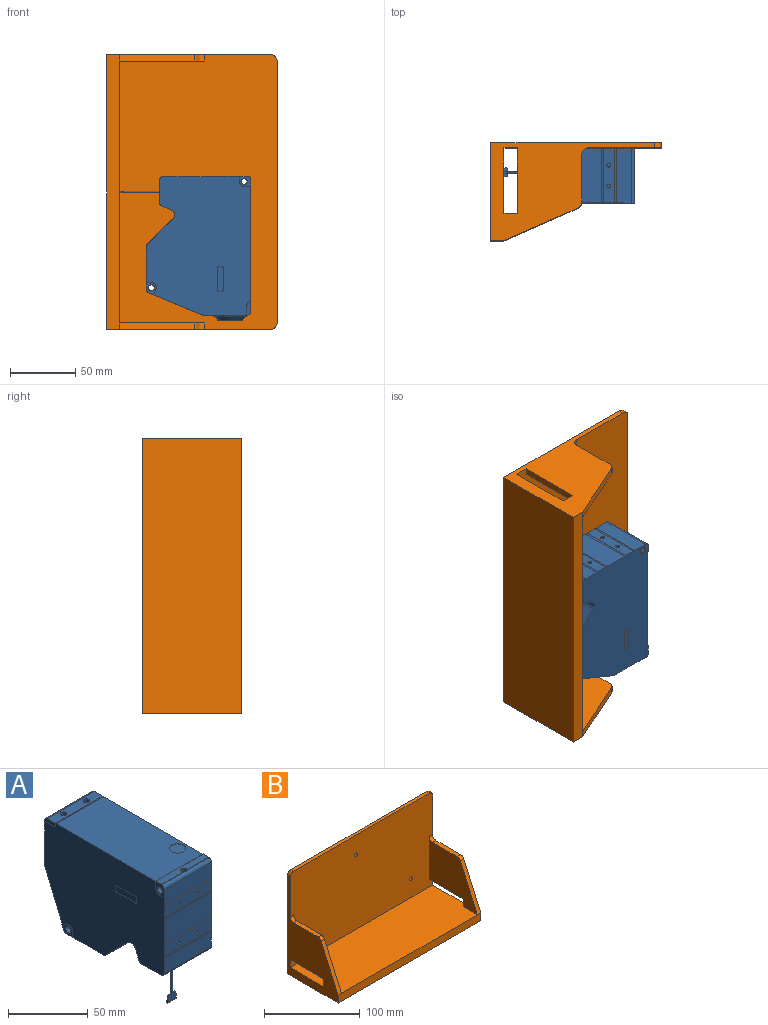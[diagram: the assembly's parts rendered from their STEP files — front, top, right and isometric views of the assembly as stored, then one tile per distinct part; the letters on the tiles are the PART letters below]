
ASSEMBLY  parts=2 mates=3
PART A: 155 faces, bbox 42x110x102.6 mm
  f0: plane 5.2x1mm, normal (-1,0,0.1), area 5.2mm2, adj f1,f4,f7,f8
  f1: plane 2.69x1mm, normal (0,0,1), area 2.6mm2, adj f0,f7,f8,f11
  f2: plane 2.69x1mm, normal (0,0,1), area 2.6mm2, adj f3,f6,f9,f11
  f3: plane 5.2x1mm, normal (1,0,0.1), area 5.2mm2, adj f2,f4,f6,f9
  f4: plane 7.5x1.5mm, normal (0,0,-1), area 7.9mm2, adj f0,f3,f6,f7,f8,f9,f11
  f5: plane 16x16mm, normal (0,1,0), area 201.1mm2, adj f10
  f6: plane 5.2x3.19mm, normal (0,1,0), area 15.3mm2, adj f2,f3,f4,f11
  f7: plane 5.2x3.19mm, normal (0,1,0), area 15.3mm2, adj f0,f1,f4,f11
  f8: plane 5.2x3.19mm, normal (0,-1,0), area 15.3mm2, adj f0,f1,f4,f11
  f9: plane 5.2x3.19mm, normal (0,-1,0), area 15.3mm2, adj f2,f3,f4,f11
  f10: cylinder r=8mm len=16mm, axis (0,-1,0), area 201.1mm2, adj f5,f12
  f11: cylinder r=0.75mm len=33.1mm, axis (0,0,1), area 144.6mm2, adj f1,f2,f4,f6,f7,f8,f9,f13
  f12: plane 18.59x18.59mm, normal (0,1,0), area 67.7mm2, adj f10,f15
  f13: plane 15x3mm, normal (0,0,-1), area 43.2mm2, adj f11,f18,f19,f20,f21
  f14: plane 20x14.14mm, normal (0,-0.71,-0.71), area 314.2mm2, adj f22
  f15: torus R=9.29mm, axis (0,-1,0), area 23.4mm2, adj f12,f23
  f16: plane 4x4mm, normal (0,0,1), area 12.6mm2, adj f25
  f17: plane 4x4mm, normal (0,0,1), area 12.6mm2, adj f26
  f18: plane 3x0.1mm, normal (-1,0,0), area 0.3mm2, adj f13,f19,f21,f39
  f19: plane 15x0.1mm, normal (0,-1,0), area 1.5mm2, adj f13,f18,f20,f39
  f20: plane 3x0.1mm, normal (1,0,0), area 0.3mm2, adj f13,f19,f21,f39
  f21: plane 15x0.1mm, normal (0,1,0), area 1.5mm2, adj f13,f18,f20,f39
  f22: cylinder r=10mm len=20mm, axis (0,-0.71,-0.71), area 6.3mm2, adj f14,f40
  f23: cone r=12.35mm half-angle=45deg, axis (0,-1,0), area 264.6mm2, adj f15,f46
  f24: plane 18.5x5mm, normal (-1,0,0), area 91.6mm2, adj f56,f57,f58,f59,f60,f61,f62,f63
  f25: cylinder r=2mm len=4.7mm, axis (0,0,1), area 59.1mm2, adj f16,f65
  f26: cylinder r=2mm len=4.7mm, axis (0,0,1), area 59.1mm2, adj f17,f65
  f27: plane 10x10mm, normal (0,0,1), area 78.5mm2, adj f68
  f28: plane 20.14x0.35mm, normal (0,-0.26,0.97), area 7.1mm2, adj f29,f32,f69,f70
  f29: cylinder r=2mm len=4.08mm, axis (0,0,1), area 42.1mm2, adj f28,f30,f31,f32,f69
  f30: plane 20.14x0.35mm, normal (0,-0.26,0.97), area 7.1mm2, adj f29,f32,f69,f71
  f31: cylinder r=2.2mm len=42mm, axis (-1,0,0), area 565.9mm2, adj f29,f70,f71
  f32: plane 42x5.01mm, normal (0,0,1), area 198.7mm2, adj f28,f29,f30,f67,f70,f71
  f33: plane 3x3mm, normal (0,-1,0), area 7.1mm2, adj f73
  f34: plane 3x3mm, normal (0,-1,0), area 7.1mm2, adj f74
  f35: plane 3x3mm, normal (0,-1,0), area 7.1mm2, adj f77
  f36: plane 3x3mm, normal (0,-1,0), area 7.1mm2, adj f78
  f37: plane 17.29x1.39mm, normal (0,0,-1), area 24mm2, adj f80,f82,f83,f84
  f38: plane 17.29x5.19mm, normal (0,0,-1), area 89.7mm2, adj f81,f85,f86,f87
  f39: plane 19.8x13.8mm, normal (0,0,-1), area 228.2mm2, adj f18,f19,f20,f21,f88,f89,f90,f91
  f40: plane 26x18.38mm, normal (0,-0.71,-0.71), area 361.8mm2, adj f22,f92,f93,f94,f95
  f41: plane 32.61x7mm, normal (0,0,-1), area 228.3mm2, adj f96,f97,f98,f99
  f42: plane 32.61x5mm, normal (0,0,-1), area 163mm2, adj f100,f101,f102,f103
  f43: plane 27.63x11.45mm, normal (0,0.92,-0.38), area 104.7mm2, adj f104,f105,f106,f107
  f44: cylinder r=2.2mm len=42mm, axis (-1,0,0), area 580.6mm2, adj f109,f110
  f45: plane 27.63x11.45mm, normal (0,0.92,-0.38), area 104.7mm2, adj f111,f112,f113,f114
  f46: torus R=12mm, axis (0,-1,0), area 30.7mm2, adj f23,f115
  f47: plane 3.81x0.2mm, normal (0,-1,0), area 0.8mm2, adj f48,f110,f116,f139
  f48: cylinder r=3.75mm len=5.18mm, axis (1,0,0), area 1.5mm2, adj f47,f49,f110,f116
  f49: plane 4.14x1.71mm, normal (0,0.38,0.92), area 0.9mm2, adj f48,f110,f116,f143
  f50: plane 8x0.2mm, normal (0,0,-1), area 1.6mm2, adj f51,f64,f116,f144
  f51: cylinder r=2mm len=2mm, axis (1,0,0), area 0.6mm2, adj f50,f52,f64,f116
  f52: plane 0.8x0.2mm, normal (0,-1,0), area 0.2mm2, adj f51,f64,f66,f116
  f53: plane 4.81x0.2mm, normal (0,1,0), area 1mm2, adj f54,f67,f71,f116
  f54: cylinder r=3.75mm len=3.75mm, axis (1,0,0), area 1.2mm2, adj f53,f55,f71,f116
  f55: plane 3.8x0.2mm, normal (0,0,-1), area 0.8mm2, adj f54,f71,f116,f127
  f56: plane 3x0.1mm, normal (0,-1,0), area 0.3mm2, adj f24,f57,f63,f116
  f57: cylinder r=1mm len=1mm, axis (-1,0,0), area 0.2mm2, adj f24,f56,f58,f116
  f58: plane 16.5x0.1mm, normal (0,0,1), area 1.6mm2, adj f24,f57,f59,f116
  f59: cylinder r=1mm len=1mm, axis (-1,0,0), area 0.2mm2, adj f24,f58,f60,f116
  f60: plane 3x0.1mm, normal (0,1,0), area 0.3mm2, adj f24,f59,f61,f116
  f61: cylinder r=1mm len=1mm, axis (-1,0,0), area 0.2mm2, adj f24,f60,f62,f116
  f62: plane 16.5x0.1mm, normal (0,0,-1), area 1.6mm2, adj f24,f61,f63,f116
  f63: cylinder r=1mm len=1mm, axis (-1,0,0), area 0.2mm2, adj f24,f56,f62,f116
  f64: plane 10x3mm, normal (-1,0,0), area 27.6mm2, adj f50,f51,f52,f65,f66,f118,f144
  f65: plane 42x7.46mm, normal (0,0,1), area 288mm2, adj f25,f26,f64,f66,f118,f119
  f66: plane 42x0.2mm, normal (0,-0.71,0.71), area 11.9mm2, adj f52,f64,f65,f119,f122,f123
  f67: plane 42x0.2mm, normal (0,0.71,0.71), area 11.9mm2, adj f32,f53,f70,f71,f123,f124
  f68: cylinder r=5mm len=10mm, axis (0,0,1), area 3.1mm2, adj f27,f123
  f69: cylinder r=2.69mm len=42mm, axis (-1,0,0), area 147mm2, adj f28,f29,f30,f70,f71,f127
  f70: plane 8.75x7.55mm, normal (1,0,0), area 46.3mm2, adj f28,f31,f32,f67,f69,f124,f125,f126
  f71: plane 8.75x7.55mm, normal (-1,0,0), area 46.3mm2, adj f30,f31,f32,f53,f54,f55,f67,f69
  f72: cylinder r=7.88mm len=41.6mm, axis (-1,0,0), area 64.6mm2, adj f116,f127,f128,f154
  f73: cylinder r=1.5mm len=3mm, axis (0,-1,0), area 28.3mm2, adj f33,f128
  f74: cylinder r=1.5mm len=3mm, axis (0,-1,0), area 28.3mm2, adj f34,f128
  f75: cylinder r=7.88mm len=41.6mm, axis (-1,0,0), area 64.6mm2, adj f116,f128,f129,f154
  f76: cylinder r=7.88mm len=41.6mm, axis (-1,0,0), area 64.6mm2, adj f116,f129,f130,f154
  f77: cylinder r=1.5mm len=3mm, axis (0,-1,0), area 28.3mm2, adj f35,f130
  f78: cylinder r=1.5mm len=3mm, axis (0,-1,0), area 28.3mm2, adj f36,f130
  f79: cylinder r=7.88mm len=41.6mm, axis (-1,0,0), area 64.6mm2, adj f116,f130,f131,f154
  f80: plane 1.39x0.2mm, normal (0,-1,0), area 0.3mm2, adj f37,f82,f84,f132
  f81: plane 5.19x0.2mm, normal (0,-1,0), area 1mm2, adj f38,f85,f87,f132
  f82: plane 17.29x0.2mm, normal (-1,0,0), area 3.5mm2, adj f37,f80,f83,f133
  f83: plane 1.39x0.2mm, normal (0,1,0), area 0.3mm2, adj f37,f82,f84,f133
  f84: plane 17.29x0.2mm, normal (1,0,0), area 3.5mm2, adj f37,f80,f83,f133
  f85: plane 17.29x0.2mm, normal (-1,0,0), area 3.5mm2, adj f38,f81,f86,f133
  f86: plane 5.19x0.2mm, normal (0,1,0), area 1mm2, adj f38,f85,f87,f133
  f87: plane 17.29x0.2mm, normal (1,0,0), area 3.5mm2, adj f38,f81,f86,f133
  f88: plane 13.8x0.2mm, normal (-1,0,0), area 2.8mm2, adj f39,f89,f91,f133
  f89: plane 19.8x0.2mm, normal (0,1,0), area 4mm2, adj f39,f88,f90,f133
  f90: plane 13.8x0.2mm, normal (1,0,0), area 2.8mm2, adj f39,f89,f91,f133
  f91: plane 19.8x0.2mm, normal (0,-1,0), area 4mm2, adj f39,f88,f90,f133
  f92: plane 18.46x18.46mm, normal (1,0,0), area 2.6mm2, adj f40,f93,f95,f137
  f93: plane 26x0.07mm, normal (0,-0.71,0.71), area 2.6mm2, adj f40,f92,f94,f137
  f94: plane 18.46x18.46mm, normal (-1,0,0), area 2.6mm2, adj f40,f93,f95,f137
  f95: plane 26x0.07mm, normal (0,0.71,-0.71), area 2.6mm2, adj f40,f92,f94,f137
  f96: plane 7x0.2mm, normal (0,-1,0), area 1.4mm2, adj f41,f97,f99,f139
  f97: plane 32.61x0.2mm, normal (-1,0,0), area 6.5mm2, adj f41,f96,f98,f139
  f98: plane 7x0.2mm, normal (0,1,0), area 1.4mm2, adj f41,f97,f99,f139
  f99: plane 32.61x0.2mm, normal (1,0,0), area 6.5mm2, adj f41,f96,f98,f139
  f100: plane 32.61x0.2mm, normal (-1,0,0), area 6.5mm2, adj f42,f101,f103,f139
  f101: plane 5x0.2mm, normal (0,1,0), area 1mm2, adj f42,f100,f102,f139
  f102: plane 32.61x0.2mm, normal (1,0,0), area 6.5mm2, adj f42,f101,f103,f139
  f103: plane 5x0.2mm, normal (0,-1,0), area 1mm2, adj f42,f100,f102,f139
  f104: plane 27.71x11.63mm, normal (-1,0,0), area 6mm2, adj f43,f105,f107,f143
  f105: plane 3.5x0.18mm, normal (0,0.38,0.92), area 0.7mm2, adj f43,f104,f106,f143
  f106: plane 27.71x11.63mm, normal (1,0,0), area 6mm2, adj f43,f105,f107,f143
  f107: plane 3.5x0.18mm, normal (0,-0.38,-0.92), area 0.7mm2, adj f43,f104,f106,f143
  f108: cylinder r=2.7mm len=42mm, axis (-1,0,0), area 133.6mm2, adj f109,f110,f139,f143
  f109: plane 9.32x7.55mm, normal (1,0,0), area 40.3mm2, adj f44,f108,f139,f140,f141,f142,f143
  f110: plane 9.32x7.55mm, normal (-1,0,0), area 40.3mm2, adj f44,f47,f48,f49,f108,f139,f143
  f111: plane 3.5x0.18mm, normal (0,-0.38,-0.92), area 0.7mm2, adj f45,f112,f114,f143
  f112: plane 27.71x11.63mm, normal (-1,0,0), area 6mm2, adj f45,f111,f113,f143
  f113: plane 3.5x0.18mm, normal (0,0.38,0.92), area 0.7mm2, adj f45,f112,f114,f143
  f114: plane 27.71x11.63mm, normal (1,0,0), area 6mm2, adj f45,f111,f113,f143
  f115: cylinder r=12.5mm len=25mm, axis (0,-1,0), area 62.3mm2, adj f46,f144
  f116: plane 106x79.6mm, normal (-1,0,0), area 7188.1mm2, adj f47,f48,f49,f50,f51,f52,f53,f54
  f117: cylinder r=2.7mm len=41.6mm, axis (-1,0,0), area 44.1mm2, adj f116,f143,f144,f154
  f118: cylinder r=2.74mm len=42mm, axis (-1,0,0), area 163.6mm2, adj f64,f65,f119,f144
  f119: plane 10x3mm, normal (1,0,0), area 27.6mm2, adj f65,f66,f118,f121,f122,f144,f145
  f120: plane 18.5x5mm, normal (1,0,0), area 91.6mm2, adj f146,f147,f148,f149,f150,f151,f152,f153
  f121: cylinder r=2mm len=2mm, axis (-1,0,0), area 0.6mm2, adj f119,f122,f145,f154
  f122: plane 0.8x0.2mm, normal (0,-1,0), area 0.2mm2, adj f66,f119,f121,f154
  f123: plane 88.25x41.6mm, normal (0,0,1), area 3592.7mm2, adj f66,f67,f68,f116,f154
  f124: plane 4.81x0.2mm, normal (0,1,0), area 1mm2, adj f67,f70,f125,f154
  f125: cylinder r=3.75mm len=3.75mm, axis (-1,0,0), area 1.2mm2, adj f70,f124,f126,f154
  f126: plane 3.8x0.2mm, normal (0,0,-1), area 0.8mm2, adj f70,f125,f127,f154
  f127: plane 42x11.69mm, normal (0,-1,0), area 488.5mm2, adj f55,f69,f70,f71,f72,f116,f126,f154
  f128: plane 41.6x8.21mm, normal (0,-1,0), area 327.5mm2, adj f72,f73,f74,f75,f116,f154
  f129: plane 41.6x18.71mm, normal (0,-1,0), area 778.5mm2, adj f75,f76,f116,f154
  f130: plane 41.6x8.21mm, normal (0,-1,0), area 327.5mm2, adj f76,f77,f78,f79,f116,f154
  f131: plane 41.6x11.46mm, normal (0,-1,0), area 476.6mm2, adj f79,f116,f132,f154
  f132: cylinder r=2.7mm len=41.6mm, axis (1,0,0), area 176.4mm2, adj f80,f81,f116,f131,f133,f154
  f133: plane 41.6x17.29mm, normal (0,0,-1), area 332.4mm2, adj f82,f83,f84,f85,f86,f87,f88,f89
  f134: cylinder r=2.7mm len=41.6mm, axis (-1,0,0), area 132.3mm2, adj f116,f133,f135,f154
  f135: plane 41.6x7.46mm, normal (0,0.92,-0.38), area 336mm2, adj f116,f134,f136,f154
  f136: cylinder r=4mm len=41.6mm, axis (-1,0,0), area 326.7mm2, adj f116,f135,f137,f154
  f137: plane 41.6x19.64mm, normal (0,-0.71,-0.71), area 479.2mm2, adj f92,f93,f94,f95,f116,f136,f138,f154
  f138: cylinder r=2.7mm len=41.6mm, axis (-1,0,0), area 88.2mm2, adj f116,f137,f139,f154
  f139: plane 42x32.62mm, normal (0,0,-1), area 967.7mm2, adj f47,f96,f97,f98,f99,f100,f101,f102
  f140: plane 3.81x0.2mm, normal (0,-1,0), area 0.8mm2, adj f109,f139,f141,f154
  f141: cylinder r=3.75mm len=5.18mm, axis (-1,0,0), area 1.5mm2, adj f109,f140,f142,f154
  f142: plane 4.14x1.71mm, normal (0,0.38,0.92), area 0.9mm2, adj f109,f141,f143,f154
  f143: plane 42x40.64mm, normal (0,0.92,-0.38), area 1622.1mm2, adj f49,f104,f105,f106,f107,f108,f109,f110
  f144: plane 42x33.76mm, normal (0,1,0), area 913.8mm2, adj f50,f64,f115,f116,f117,f118,f119,f145
  f145: plane 8x0.2mm, normal (0,0,-1), area 1.6mm2, adj f119,f121,f144,f154
  f146: cylinder r=1mm len=1mm, axis (1,0,0), area 0.2mm2, adj f120,f147,f153,f154
  f147: plane 16.5x0.1mm, normal (0,0,1), area 1.6mm2, adj f120,f146,f148,f154
  f148: cylinder r=1mm len=1mm, axis (1,0,0), area 0.2mm2, adj f120,f147,f149,f154
  f149: plane 3x0.1mm, normal (0,1,0), area 0.3mm2, adj f120,f148,f150,f154
  f150: cylinder r=1mm len=1mm, axis (1,0,0), area 0.2mm2, adj f120,f149,f151,f154
  f151: plane 16.5x0.1mm, normal (0,0,-1), area 1.7mm2, adj f120,f150,f152,f154
  f152: cylinder r=1mm len=1mm, axis (1,0,0), area 0.2mm2, adj f120,f151,f153,f154
  f153: plane 3x0.1mm, normal (0,-1,0), area 0.3mm2, adj f120,f146,f152,f154
  f154: plane 106x79.6mm, normal (1,0,0), area 7188.1mm2, adj f72,f75,f76,f79,f117,f121,f122,f123
PART B: 26 faces, bbox 210x75x130 mm
  f0: plane 210x120mm, normal (0,-1,0), area 24613.9mm2, adj f2,f4,f5,f6,f7,f10,f14,f17
  f1: plane 210x130mm, normal (0,1,0), area 27258.9mm2, adj f2,f4,f9,f17,f18,f19,f20,f21
  f2: plane 125x75mm, normal (1,0,0), area 4152.5mm2, adj f0,f1,f7,f8,f9,f12,f13,f14
  f3: plane 56.53x25.08mm, normal (0,-0.91,0.41), area 309.2mm2, adj f4,f5,f8,f25
  f4: plane 125x75mm, normal (-1,0,0), area 4152.5mm2, adj f0,f1,f3,f7,f8,f9,f10,f11
  f5: plane 71x64.5mm, normal (1,0,0), area 2942.5mm2, adj f0,f3,f7,f10,f11,f16,f24,f25
  f6: plane 71x64.5mm, normal (-1,0,0), area 2942.5mm2, adj f0,f7,f12,f13,f14,f15,f22,f23
  f7: plane 210x71mm, normal (0,0,1), area 14700mm2, adj f0,f2,f4,f5,f6,f8,f11,f13
  f8: plane 210x10mm, normal (0,-1,0), area 2100mm2, adj f2,f3,f4,f7,f9,f12
  f9: plane 210x75mm, normal (0,0,-1), area 15750mm2, adj f1,f2,f4,f8
  f10: plane 50x5mm, normal (0,0,-1), area 250mm2, adj f0,f4,f5,f11
  f11: plane 10x5mm, normal (0,1,0), area 50mm2, adj f4,f5,f7,f10
  f12: plane 56.53x25.08mm, normal (0,-0.91,0.41), area 309.2mm2, adj f2,f6,f8,f23
  f13: plane 10x5mm, normal (0,1,0), area 50mm2, adj f2,f6,f7,f14
  f14: plane 50x5mm, normal (0,0,-1), area 250mm2, adj f0,f2,f6,f13
  f15: plane 36.35x5mm, normal (0,0,1), area 181.7mm2, adj f2,f6,f22,f23
  f16: plane 36.35x5mm, normal (0,0,1), area 181.7mm2, adj f4,f5,f24,f25
  f17: cylinder r=2.2mm len=4.4mm, axis (0,-1,0), area 55.3mm2, adj f0,f1
  f18: cylinder r=2.2mm len=4.4mm, axis (0,-1,0), area 55.3mm2, adj f0,f1
  f19: plane 200x4mm, normal (0,0,1), area 800mm2, adj f0,f1,f20,f21
  f20: cylinder r=5mm len=5mm, axis (0,1,0), area 31.4mm2, adj f0,f1,f4,f19
  f21: cylinder r=5mm len=5mm, axis (0,-1,0), area 31.4mm2, adj f0,f1,f2,f19
  f22: cylinder r=5mm len=5mm, axis (-1,0,0), area 39.3mm2, adj f0,f2,f6,f15
  f23: cylinder r=5mm len=5mm, axis (1,0,0), area 28.8mm2, adj f2,f6,f12,f15
  f24: cylinder r=5mm len=5mm, axis (-1,0,0), area 39.3mm2, adj f0,f4,f5,f16
  f25: cylinder r=5mm len=5mm, axis (-1,0,0), area 28.8mm2, adj f3,f4,f5,f16
PLACE A rot(axis=(-0.58,0.58,-0.58),120deg) t=(-22.95,81.45,41.74)mm
PLACE B rot(axis=(0,1,0),90deg) t=(57.05,106.45,41.74)mm
MATE fastened A.f31 <-> B.f18  axis (0,1,0) through (72.05,102.45,49.74)mm
MATE parallel B.f5 <-> A.f129  axis (0,0,-1) through (8.39,72.36,141.74)mm
MATE parallel A.f116 <-> B.f0  axis (0,1,0) through (40.85,102.25,0.54)mm
